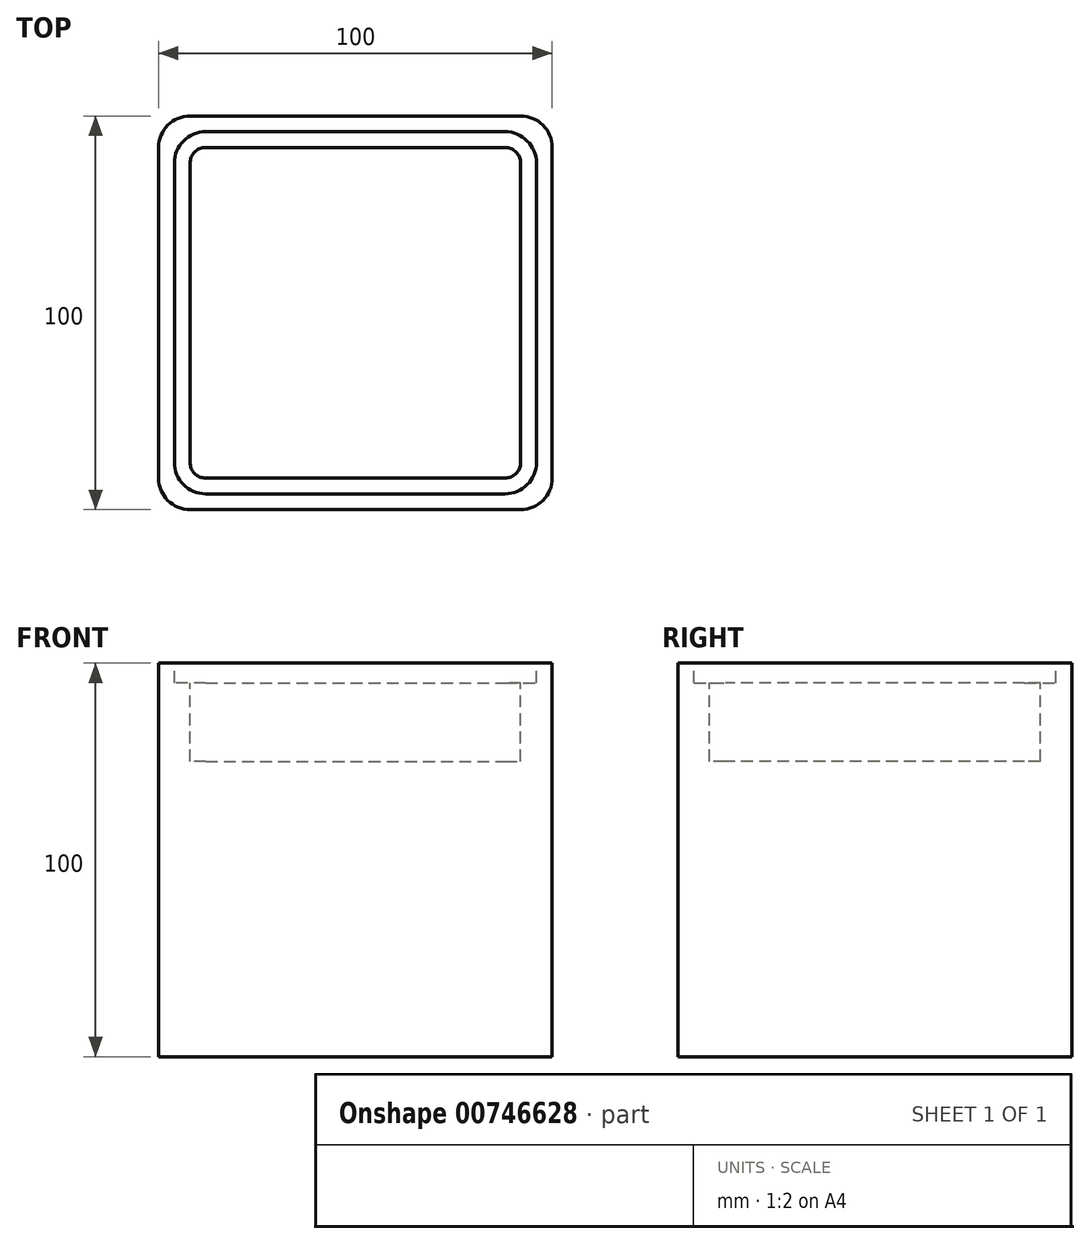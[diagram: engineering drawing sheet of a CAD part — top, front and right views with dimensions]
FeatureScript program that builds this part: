
annotation { "Feature Type Name" : "Feature", "Feature Type Description" : "" }
export const myFeature = defineFeature(function(context is Context, id is Id, definition is map)
    precondition{}
    {
        {
            var Q0;
            Q0=qCreatedBy(makeId("Top.planeOp"),FACE);
            var sketch = newSketch(context, id + "F0", { "sketchPlane" : qUnion([Q0])});
            skLineSegment(sketch, "E0.bottom", {"start": v(-42, 50) * mm, "end": v(42, 50) * mm});
            skLineSegment(sketch, "E0.top", {"start": v(-42, -50) * mm, "end": v(42, -50) * mm});
            skLineSegment(sketch, "E0.left", {"start": v(-50, 42) * mm, "end": v(-50, -42) * mm});
            skLineSegment(sketch, "E0.right", {"start": v(50, 42) * mm, "end": v(50, -42) * mm});
            skPoint(sketch, "E1.visualSharp", {"position": v(50, 50) * mm});
            skArc(sketch, "E1.filletArc", {"start": v(50, 42) * mm, "mid": v(47.66, 47.66) * mm, "end": v(42, 50) * mm});
            skPoint(sketch, "E2.visualSharp", {"position": v(50, -50) * mm});
            skArc(sketch, "E2.filletArc", {"start": v(42, -50) * mm, "mid": v(47.66, -47.66) * mm, "end": v(50, -42) * mm});
            skPoint(sketch, "E3.visualSharp", {"position": v(-50, 50) * mm});
            skArc(sketch, "E3.filletArc", {"start": v(-42, 50) * mm, "mid": v(-47.66, 47.66) * mm, "end": v(-50, 42) * mm});
            skPoint(sketch, "E4.visualSharp", {"position": v(-50, -50) * mm});
            skArc(sketch, "E4.filletArc", {"start": v(-50, -42) * mm, "mid": v(-47.66, -47.66) * mm, "end": v(-42, -50) * mm});
            skSolve(sketch);
        }
        {
            var Q0;
            Q0=makeQuery(id+"F0.imprint","IMPRINT",FACE,{"disambiguationData":[TD([[makeQuery(id+"F0.imprint","IMPRINT",EDGE,{"derivedFrom":sQuery(id+"F0.wireOp",EDGE,"E0.bottom")}),-1.0]])]});
            extrude(context, id + "F1", {"entities" : qUnion([Q0]), "depth" : 100 * mm, "offsetDistance" : 25 * mm});
        }
        {
            var Q0;
            Q0=makeQuery(id+"F1.opExtrude","CAP_FACE",FACE,{"disambiguationData":[OSD([sQuery(id+"F0.wireOp",EDGE,"E0.bottom"),sQuery(id+"F0.wireOp",EDGE,"E0.top"),sQuery(id+"F0.wireOp",EDGE,"E0.left"),sQuery(id+"F0.wireOp",EDGE,"E0.right"),sQuery(id+"F0.wireOp",EDGE,"E1.filletArc"),sQuery(id+"F0.wireOp",EDGE,"E2.filletArc"),sQuery(id+"F0.wireOp",EDGE,"E3.filletArc"),sQuery(id+"F0.wireOp",EDGE,"E4.filletArc")])],"isStart":false});
            var sketch = newSketch(context, id + "F2", { "sketchPlane" : qUnion([Q0])});
            skLineSegment(sketch, "E5.0", {"start": v(46, 38) * mm, "end": v(46, -38) * mm});
            skLineSegment(sketch, "E5.1", {"start": v(-38, 46) * mm, "end": v(38, 46) * mm});
            skLineSegment(sketch, "E5.2", {"start": v(-46, 38) * mm, "end": v(-46, -38) * mm});
            skLineSegment(sketch, "E5.3", {"start": v(-38, -46) * mm, "end": v(38, -46) * mm});
            skPoint(sketch, "E6.visualSharp", {"position": v(46, 46) * mm});
            skArc(sketch, "E6.filletArc", {"start": v(46, 38) * mm, "mid": v(43.66, 43.66) * mm, "end": v(38, 46) * mm});
            skPoint(sketch, "E7.visualSharp", {"position": v(46, -46) * mm});
            skArc(sketch, "E7.filletArc", {"start": v(38, -46) * mm, "mid": v(43.66, -43.66) * mm, "end": v(46, -38) * mm});
            skPoint(sketch, "E8.visualSharp", {"position": v(-46, -46) * mm});
            skArc(sketch, "E8.filletArc", {"start": v(-46, -38) * mm, "mid": v(-43.66, -43.66) * mm, "end": v(-38, -46) * mm});
            skPoint(sketch, "E9.visualSharp", {"position": v(-46, 46) * mm});
            skArc(sketch, "E9.filletArc", {"start": v(-38, 46) * mm, "mid": v(-43.66, 43.66) * mm, "end": v(-46, 38) * mm});
            skSolve(sketch);
        }
        {
            var Q0;
            Q0=makeQuery(id+"F2.imprint","IMPRINT",FACE,{"disambiguationData":[TD([[makeQuery(id+"F2.imprint","IMPRINT",EDGE,{"derivedFrom":sQuery(id+"F2.wireOp",EDGE,"E5.0")}),-1.0]])]});
            extrude(context, id + "F3", {"entities" : qUnion([Q0]), "operationType" : NewBodyOperationType.REMOVE, "oppositeDirection" : true, "depth" : 5 * mm, "offsetDistance" : 25 * mm});
        }
        {
            var Q0;
            Q0=makeQuery(id+"F3.boolean.opBoolean","COPY",FACE,{"derivedFrom":makeQuery(id+"F3.opExtrude","CAP_FACE",FACE,{"disambiguationData":[OSD([sQuery(id+"F2.wireOp",EDGE,"E5.0"),sQuery(id+"F2.wireOp",EDGE,"E5.1"),sQuery(id+"F2.wireOp",EDGE,"E5.2"),sQuery(id+"F2.wireOp",EDGE,"E5.3"),sQuery(id+"F2.wireOp",EDGE,"E6.filletArc"),sQuery(id+"F2.wireOp",EDGE,"E7.filletArc"),sQuery(id+"F2.wireOp",EDGE,"E8.filletArc"),sQuery(id+"F2.wireOp",EDGE,"E9.filletArc")])],"isStart":false})});
            var sketch = newSketch(context, id + "F4", { "sketchPlane" : qUnion([Q0])});
            skLineSegment(sketch, "E10.0", {"start": v(-38, 46) * mm, "end": v(38, 46) * mm, "construction": true});
            skArc(sketch, "E11.0", {"start": v(-38, 46) * mm, "mid": v(-43.66, 43.66) * mm, "end": v(-46, 38) * mm, "construction": true});
            skLineSegment(sketch, "E12.0", {"start": v(-46, 38) * mm, "end": v(-46, -38) * mm, "construction": true});
            skArc(sketch, "E13.0", {"start": v(-46, -38) * mm, "mid": v(-43.66, -43.66) * mm, "end": v(-38, -46) * mm, "construction": true});
            skArc(sketch, "E14.0", {"start": v(38, -46) * mm, "mid": v(43.66, -43.66) * mm, "end": v(46, -38) * mm, "construction": true});
            skLineSegment(sketch, "E14.1", {"start": v(-38, -46) * mm, "end": v(38, -46) * mm, "construction": true});
            skLineSegment(sketch, "E14.2", {"start": v(46, 38) * mm, "end": v(46, -38) * mm, "construction": true});
            skArc(sketch, "E15.0", {"start": v(46, 38) * mm, "mid": v(43.66, 43.66) * mm, "end": v(38, 46) * mm, "construction": true});
            skArc(sketch, "E16.0", {"start": v(-38, 42) * mm, "mid": v(-40.83, 40.83) * mm, "end": v(-42, 38) * mm});
            skLineSegment(sketch, "E16.1", {"start": v(-38, 42) * mm, "end": v(38, 42) * mm});
            skLineSegment(sketch, "E16.2", {"start": v(-42, 38) * mm, "end": v(-42, -38) * mm});
            skArc(sketch, "E16.3", {"start": v(42, 38) * mm, "mid": v(40.83, 40.83) * mm, "end": v(38, 42) * mm});
            skArc(sketch, "E16.4", {"start": v(-42, -38) * mm, "mid": v(-40.83, -40.83) * mm, "end": v(-38, -42) * mm});
            skLineSegment(sketch, "E16.5", {"start": v(-38, -42) * mm, "end": v(38, -42) * mm});
            skArc(sketch, "E16.6", {"start": v(38, -42) * mm, "mid": v(40.83, -40.83) * mm, "end": v(42, -38) * mm});
            skLineSegment(sketch, "E16.7", {"start": v(42, 38) * mm, "end": v(42, -38) * mm});
            skSolve(sketch);
        }
        {
            var Q0;
            Q0=makeQuery(id+"F4.imprint","IMPRINT",FACE,{"disambiguationData":[TD([[makeQuery(id+"F4.imprint","IMPRINT",EDGE,{"derivedFrom":sQuery(id+"F4.wireOp",EDGE,"E16.0")}),1.0]])]});
            extrude(context, id + "F5", {"entities" : qUnion([Q0]), "operationType" : NewBodyOperationType.REMOVE, "oppositeDirection" : true, "depth" : 20 * mm, "offsetDistance" : 25 * mm});
        }
    });
